# Revit family: I Shapes Section
name_source: partatom
category: Structural Framing
revit_build: Autodesk Revit Structure 2012 (Build: 20110916_2132(x64)
units: mm (PartAtom-declared; Revit-internal decimal feet)

## types (16) — shared parameters
Assembly Code = B10

## per-type parameters (varying)
| type | A | W | bf | d | m | n | r | tw |
| 10 I 22 | 6.42 in² | 22 | 0' - 5" | 0' - 10" | 0' - 0 9/16" | 0' - 0 1/4" | 0' - 0 1/4" | 0' - 0 1/4" |
| 12 I 25 | 7.35 in² | 25 | 0' - 5" | 1' - 0" | 0' - 0 11/16" | 0' - 0 1/4" | 0' - 0 3/8" | 0' - 0 1/4" |
| 12 I 30.5 | 9.26 in² | 30.5 | 0' - 5" | 1' - 0" | 0' - 0 3/4" | 0' - 0 3/8" | 0' - 0 7/16" | 0' - 0 3/8" |
| 15 I 35 | 10.22 in² | 35 | 0' - 5 1/2" | 1' - 3" | 0' - 0 5/8" | 0' - 0 5/16" | 0' - 0 5/16" | 0' - 0 5/16" |
| 15 I 42 | 12.35 in² | 42 | 0' - 5 1/2" | 1' - 3" | 0' - 0 13/16" | 0' - 0 7/16" | 0' - 0 1/2" | 0' - 0 7/16" |
| 15 I 50 | 14.59 in² | 50 | 0' - 5 5/8" | 1' - 3" | 0' - 0 13/16" | 0' - 0 7/16" | 0' - 0 1/2" | 0' - 0 9/16" |
| 15 I 60 | 17.6 in² | 60 | 0' - 6" | 1' - 3" | 0' - 1 1/8" | 0' - 0 11/16" | 0' - 0 5/8" | 0' - 0 1/2" |
| 15 I 65 | 18.91 in² | 65 | 0' - 6 1/16" | 1' - 3" | 0' - 1 1/16" | 0' - 0 9/16" | 0' - 0 11/16" | 0' - 0 11/16" |
| 15 I 75 | 21.85 in² | 75 | 0' - 6 1/4" | 1' - 3" | 0' - 1 1/16" | 0' - 0 9/16" | 0' - 0 11/16" | 0' - 0 7/8" |
| 18 I 46 | 13.34 in² | 46 | 0' - 6" | 1' - 6" | 0' - 0 3/4" | 0' - 0 3/8" | 0' - 0 3/8" | 0' - 0 3/8" |
| 18 I 55 | 15.93 in² | 55 | 0' - 6" | 1' - 6" | 0' - 0 15/16" | 0' - 0 7/16" | 0' - 0 9/16" | 0' - 0 7/16" |
| 18 I 75 | 22.1 in² | 75 | 0' - 6 9/16" | 1' - 6" | 0' - 1 3/16" | 0' - 0 5/8" | 0' - 0 3/4" | 0' - 0 5/8" |
| 18 I 80 | 23.34 in² | 80 | 0' - 7 1/16" | 1' - 6" | 0' - 1 3/16" | 0' - 0 11/16" | 0' - 0 11/16" | 0' - 0 5/8" |
| 18 I 90 | 26.29 in² | 90 | 0' - 7 1/4" | 1' - 6" | 0' - 1 3/16" | 0' - 0 11/16" | 0' - 0 11/16" | 0' - 0 13/16" |
| 24 I 105 | 30.98 in² | 105 | 0' - 7 7/8" | 2' - 0" | 0' - 1 3/8" | 0' - 0 13/16" | 0' - 0 5/8" | 0' - 0 5/8" |
| 8 I 18 | 5.2 in² | 18 | 0' - 4 1/8" | 0' - 8" | 0' - 0 9/16" | 0' - 0 1/4" | 0' - 0 3/8" | 0' - 0 1/4" |

## geometry (parser evidence)
native form markers: Sweep x2
no freeform markers — native parametric forms only
